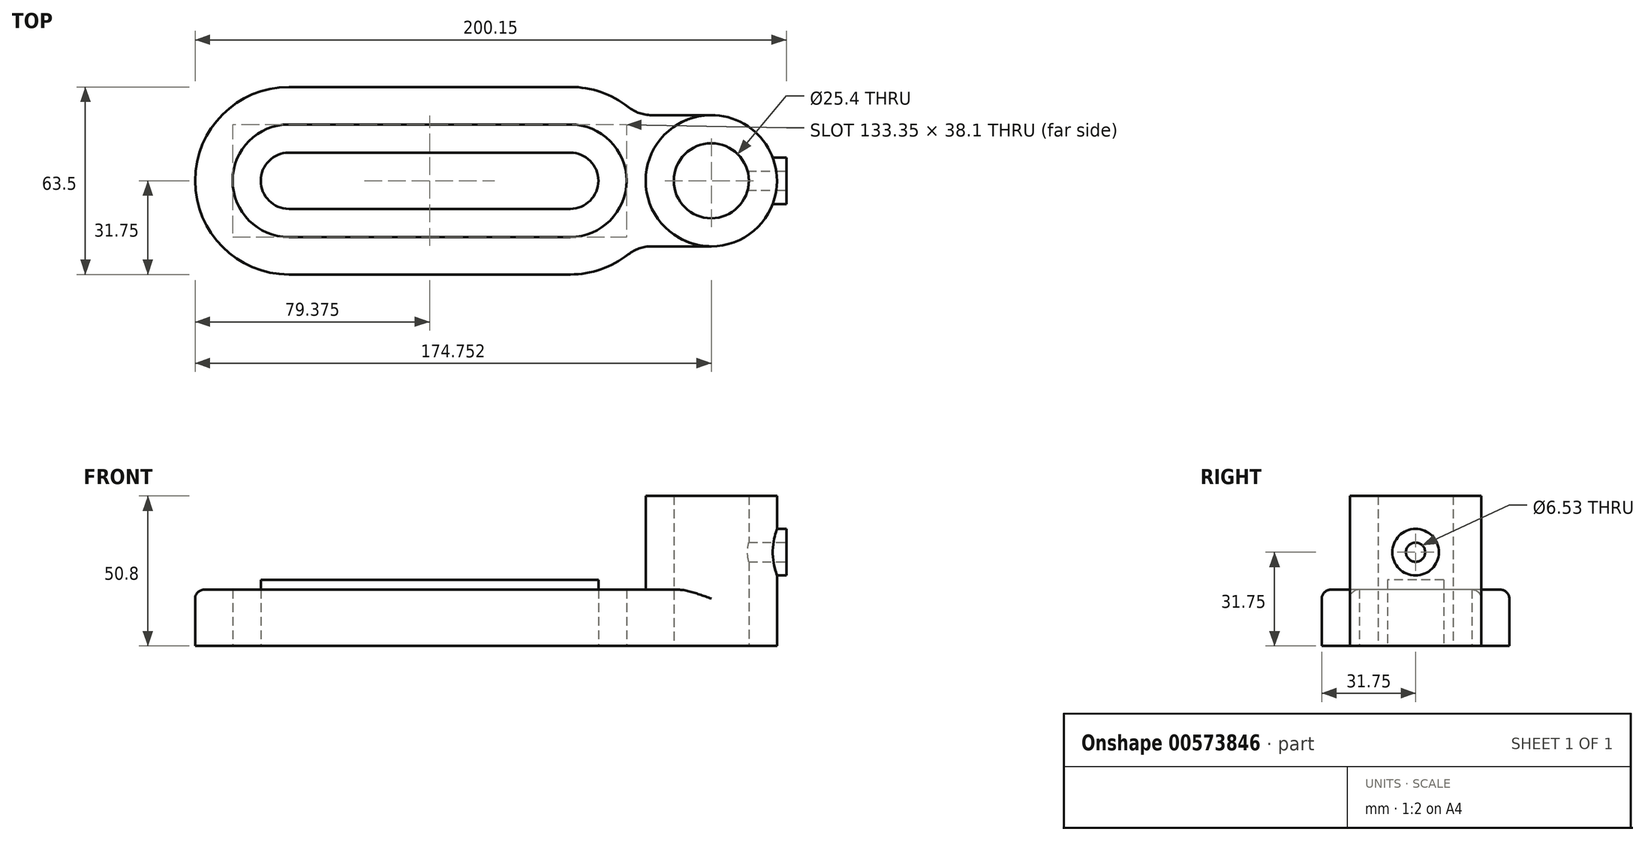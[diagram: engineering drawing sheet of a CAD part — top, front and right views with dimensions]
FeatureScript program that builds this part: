
annotation { "Feature Type Name" : "Feature", "Feature Type Description" : "" }
export const myFeature = defineFeature(function(context is Context, id is Id, definition is map)
    precondition{}
    {
        {
            var Q0;
            Q0=qCreatedBy(makeId("Top.planeOp"),FACE);
            var sketch = newSketch(context, id + "F0", { "sketchPlane" : qUnion([Q0])});
            skLineSegment(sketch, "E0", {"start": v(-95.25, 0) * mm, "end": v(73.15, 0) * mm, "construction": true});
            skPoint(sketch, "E1", {"position": v(-11.05, 0) * mm});
            skLineSegment(sketch, "E2", {"start": v(-95.25, 92.14) * mm, "end": v(-95.25, -50.35) * mm, "construction": true});
            skLineSegment(sketch, "E3", {"start": v(0, 91.82) * mm, "end": v(0, -51.6) * mm, "construction": true});
            skLineSegment(sketch, "E4", {"start": v(47.75, 93.07) * mm, "end": v(47.75, -51.91) * mm, "construction": true});
            skLineSegment(sketch, "E5", {"start": v(73.15, 93.07) * mm, "end": v(73.15, -51.91) * mm, "construction": true});
            skCircle(sketch, "E6", {"center": v(47.75, 0) * mm, "radius": 12.7 * mm});
            skCircle(sketch, "E7", {"center": v(47.75, 0) * mm, "radius": 22.23 * mm});
            skLineSegment(sketch, "E8", {"start": v(-95.25, 31.75) * mm, "end": v(0, 31.75) * mm});
            skLineSegment(sketch, "E9", {"start": v(-95.25, -31.75) * mm, "end": v(0, -31.75) * mm});
            skArc(sketch, "E10", {"start": v(-95.25, 31.75) * mm, "mid": v(-127, 0) * mm, "end": v(-95.25, -31.75) * mm});
            skLineSegment(sketch, "E11", {"start": v(-47.62, 31.75) * mm, "end": v(-47.62, -31.75) * mm, "construction": true});
            skArc(sketch, "E12.MirrorCS", {"start": v(0, 31.75) * mm, "mid": v(10.4, 30) * mm, "end": v(19.64, 24.95) * mm});
            skLineSegment(sketch, "E13", {"start": v(-95.25, 0) * mm, "end": v(0, 0) * mm, "construction": true});
            skArc(sketch, "E14.0.startCap", {"start": v(-95.25, -9.52) * mm, "mid": v(-104.78, 0) * mm, "end": v(-95.25, 9.52) * mm});
            skArc(sketch, "E14.0.endCap", {"start": v(0, 9.52) * mm, "mid": v(9.52, 0) * mm, "end": v(0, -9.52) * mm});
            skLineSegment(sketch, "E14.0.left", {"start": v(-95.25, 9.52) * mm, "end": v(0, 9.52) * mm});
            skLineSegment(sketch, "E14.0.right", {"start": v(-95.25, -9.52) * mm, "end": v(0, -9.52) * mm});
            skArc(sketch, "E15.0.startCap", {"start": v(-95.25, -19.05) * mm, "mid": v(-114.3, 0) * mm, "end": v(-95.25, 19.05) * mm});
            skArc(sketch, "E15.0.endCap", {"start": v(0, 19.05) * mm, "mid": v(19.05, 0) * mm, "end": v(0, -19.05) * mm});
            skLineSegment(sketch, "E15.0.left", {"start": v(-95.25, 19.05) * mm, "end": v(0, 19.05) * mm});
            skLineSegment(sketch, "E15.0.right", {"start": v(-95.25, -19.05) * mm, "end": v(0, -19.05) * mm});
            skLineSegment(sketch, "E16", {"start": v(47.75, 22.23) * mm, "end": v(27.5, 22.23) * mm});
            skPoint(sketch, "E16.startSnap0", {"position": v(47.75, 20.58) * mm});
            skLineSegment(sketch, "E17", {"start": v(47.75, -22.23) * mm, "end": v(27.5, -22.23) * mm});
            skArc(sketch, "E18.trimOffspring", {"start": v(19.64, -24.95) * mm, "mid": v(10.4, -30) * mm, "end": v(0, -31.75) * mm});
            skPoint(sketch, "E19.visualSharp", {"position": v(22.67, 22.23) * mm});
            skArc(sketch, "E19.filletArc", {"start": v(19.64, 24.95) * mm, "mid": v(23.34, 22.92) * mm, "end": v(27.5, 22.23) * mm});
            skPoint(sketch, "E20.visualSharp", {"position": v(22.67, -22.23) * mm});
            skArc(sketch, "E20.filletArc", {"start": v(27.5, -22.23) * mm, "mid": v(23.34, -22.92) * mm, "end": v(19.64, -24.95) * mm});
            skSolve(sketch);
        }
        {
            var Q0;
            Q0=makeQuery(id+"F0.imprint","IMPRINT",FACE,{"disambiguationData":[TD([[makeQuery(id+"F0.imprint","IMPRINT",EDGE,{"derivedFrom":sQuery(id+"F0.wireOp",EDGE,"E8")}),-1.0]])]});
            var Q1;
            Q1=makeQuery(id+"F0.imprint","IMPRINT",FACE,{"disambiguationData":[TD([[makeQuery(id+"F0.imprint","IMPRINT",EDGE,{"derivedFrom":sQuery(id+"F0.wireOp",EDGE,"E14.0.startCap")}),1.0]])]});
            var Q2;
            Q2=makeQuery(id+"F0.imprint","IMPRINT",FACE,{"disambiguationData":[TD([[makeQuery(id+"F0.imprint","IMPRINT",EDGE,{"derivedFrom":sQuery(id+"F0.wireOp",EDGE,"E6")}),-1.0]])]});
            extrude(context, id + "F1", {"entities" : qUnion([Q0, Q1, Q2]), "depth" : 19.05 * mm, "offsetDistance" : 25.4 * mm});
        }
        {
            var Q0;
            Q0=makeQuery(id+"F0.imprint","IMPRINT",FACE,{"disambiguationData":[TD([[makeQuery(id+"F0.imprint","IMPRINT",EDGE,{"derivedFrom":sQuery(id+"F0.wireOp",EDGE,"E14.0.startCap")}),1.0]])]});
            extrude(context, id + "F2", {"entities" : qUnion([Q0]), "operationType" : NewBodyOperationType.ADD, "depth" : 22.35 * mm, "offsetDistance" : 25.4 * mm});
        }
        {
            var Q0;
            Q0=makeQuery(id+"F0.imprint","IMPRINT",FACE,{"disambiguationData":[TD([[makeQuery(id+"F0.imprint","IMPRINT",EDGE,{"derivedFrom":sQuery(id+"F0.wireOp",EDGE,"E6")}),-1.0]])]});
            extrude(context, id + "F3", {"entities" : qUnion([Q0]), "operationType" : NewBodyOperationType.ADD, "depth" : 50.8 * mm, "offsetDistance" : 25.4 * mm});
        }
        {
            var Q0;
            Q0=qCreatedBy(makeId("Right.planeOp"),FACE);
            cPlane(context, id + "F4", {"entities" : qUnion([Q0]), "cplaneType" : CPlaneType.OFFSET, "offset" : 73.15 * mm, "width" : 152.4 * mm, "height" : 152.4 * mm});
        }
        {
            var Q0;
            Q0=qCreatedBy(id+"F4.planeOp",FACE);
            var sketch = newSketch(context, id + "F5", { "sketchPlane" : qUnion([Q0])});
            skCircle(sketch, "E21", {"center": v(0, 31.75) * mm, "radius": 7.87 * mm});
            skCircle(sketch, "E22", {"center": v(0, 31.75) * mm, "radius": 3.26 * mm});
            skSolve(sketch);
        }
        {
            var Q0;
            Q0=makeQuery(id+"F5.imprint","IMPRINT",FACE,{"disambiguationData":[TD([[makeQuery(id+"F5.imprint","IMPRINT",EDGE,{"derivedFrom":sQuery(id+"F5.wireOp",EDGE,"E21")}),1.0]])]});
            extrude(context, id + "F6", {"entities" : qUnion([Q0]), "operationType" : NewBodyOperationType.ADD, "endBound" : BoundingType.UP_TO_NEXT, "oppositeDirection" : true, "depth" : 25.4 * mm, "offsetDistance" : 25.4 * mm});
        }
        {
            var Q0;
            Q0=makeQuery(id+"F5.imprint","IMPRINT",FACE,{"disambiguationData":[TD([[makeQuery(id+"F5.imprint","IMPRINT",EDGE,{"derivedFrom":sQuery(id+"F5.wireOp",EDGE,"E22")}),1.0]])]});
            extrude(context, id + "F7", {"entities" : qUnion([Q0]), "operationType" : NewBodyOperationType.REMOVE, "oppositeDirection" : true, "depth" : 25.4 * mm, "offsetDistance" : 25.4 * mm});
        }
        {
            var Q0;
            Q0=makeQuery(id+"F2.boolean.opBoolean","INTERSECT",EDGE,{"derivedFrom":[makeQuery(id+"F1.opExtrude","CAP_FACE",FACE,{"disambiguationData":[OSD([sQuery(id+"F0.wireOp",EDGE,"E6"),sQuery(id+"F0.wireOp",EDGE,"E7"),sQuery(id+"F0.wireOp",EDGE,"E8"),sQuery(id+"F0.wireOp",EDGE,"E9"),sQuery(id+"F0.wireOp",EDGE,"E10"),sQuery(id+"F0.wireOp",EDGE,"E12.MirrorCS"),sQuery(id+"F0.wireOp",EDGE,"E14.0.startCap"),sQuery(id+"F0.wireOp",EDGE,"E14.0.endCap"),sQuery(id+"F0.wireOp",EDGE,"E14.0.left"),sQuery(id+"F0.wireOp",EDGE,"E14.0.right"),sQuery(id+"F0.wireOp",EDGE,"E16"),sQuery(id+"F0.wireOp",EDGE,"E17"),sQuery(id+"F0.wireOp",EDGE,"E18.trimOffspring"),sQuery(id+"F0.wireOp",EDGE,"E19.filletArc"),sQuery(id+"F0.wireOp",EDGE,"E20.filletArc")])],"isStart":false}),makeQuery(id+"F2.opExtrude","SWEPT_FACE",FACE,{"disambiguationData":[OSD([sQuery(id+"F0.wireOp",EDGE,"E15.0.right")])]})]});
            var Q1;
            Q1=makeQuery(id+"F6.opExtrude","CAP_EDGE",EDGE,{"disambiguationData":[OSD([sQuery(id+"F5.wireOp",EDGE,"E21")])],"isStart":false});
            var Q2;
            Q2=makeQuery(id+"F1.opExtrude","CAP_EDGE",EDGE,{"disambiguationData":[OSD([sQuery(id+"F0.wireOp",EDGE,"E9")])],"isStart":false});
            fillet(context, id + "F8", {"entities" : qUnion([Q0, Q1, Q2]), "radius" : 3.05 * mm, "tangentPropagation" : true, "allowEdgeOverflow" : false});
        }
    });
